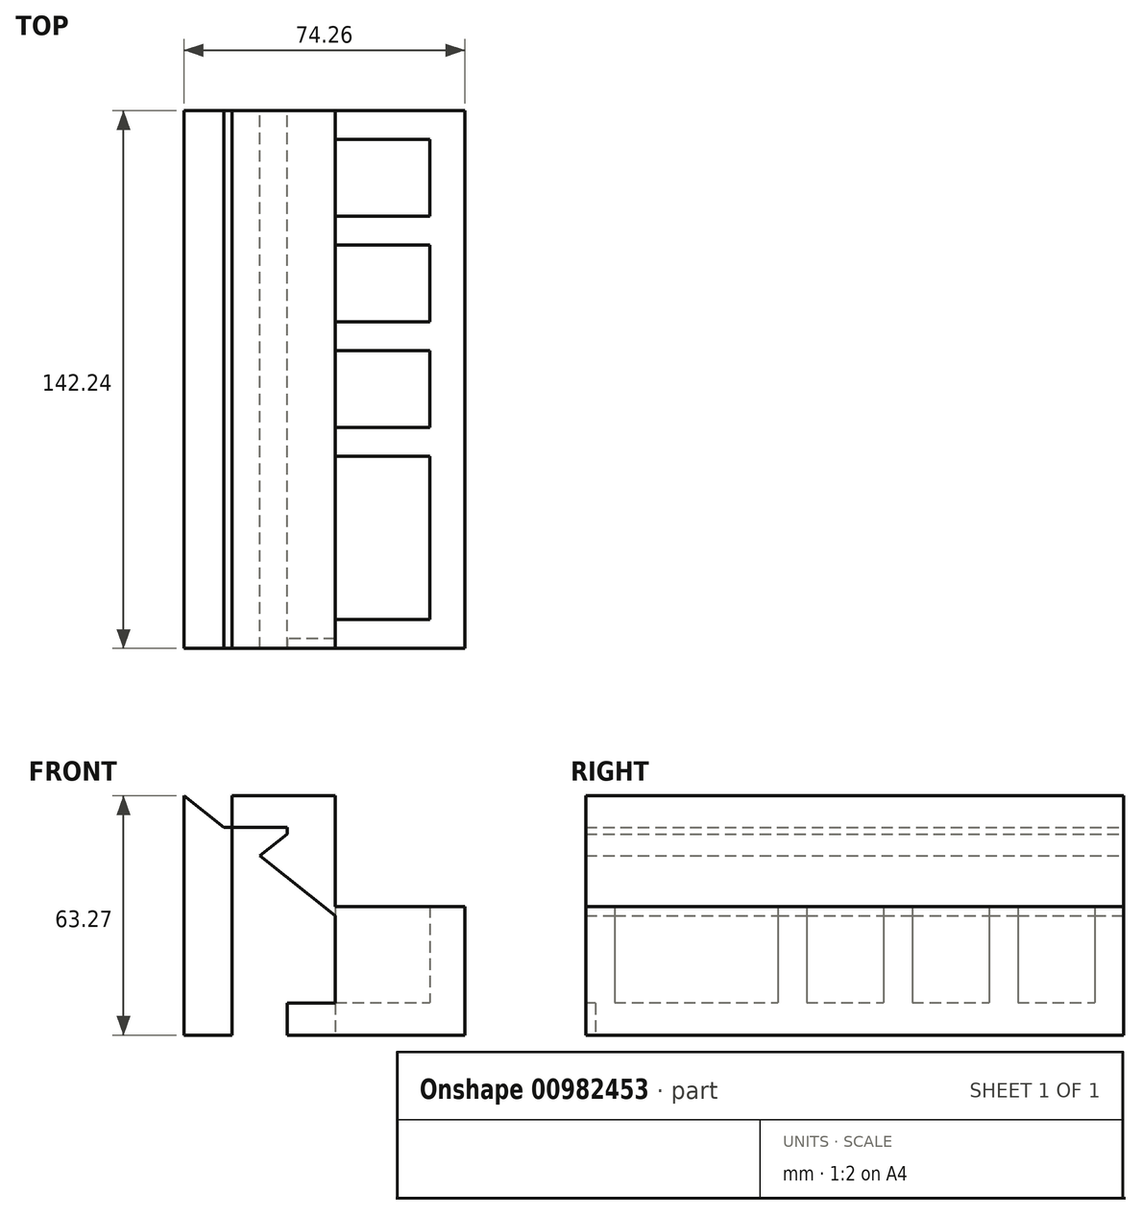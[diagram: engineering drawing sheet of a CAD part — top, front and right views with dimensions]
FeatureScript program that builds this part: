
annotation { "Feature Type Name" : "Feature", "Feature Type Description" : "" }
export const myFeature = defineFeature(function(context is Context, id is Id, definition is map)
    precondition{}
    {
        {
            var Q0;
            Q0=qCreatedBy(makeId("Front.planeOp"),FACE);
            var sketch = newSketch(context, id + "F0", { "sketchPlane" : qUnion([Q0])});
            skLineSegment(sketch, "E0.bottom", {"start": v(-54.43, 16.05) * mm, "end": v(-67.13, 16.05) * mm});
            skLineSegment(sketch, "E0.top", {"start": v(-54.43, 63.27) * mm, "end": v(-67.13, 63.27) * mm});
            skLineSegment(sketch, "E0.left", {"start": v(-54.43, 16.05) * mm, "end": v(-54.43, 63.27) * mm});
            skLineSegment(sketch, "E0.right", {"start": v(-67.13, 16.05) * mm, "end": v(-67.13, 63.27) * mm});
            skLineSegment(sketch, "E1.bottom", {"start": v(-67.13, 63.27) * mm, "end": v(-27.13, 63.27) * mm});
            skLineSegment(sketch, "E1.top", {"start": v(-67.13, 54.94) * mm, "end": v(-27.13, 54.94) * mm});
            skLineSegment(sketch, "E1.left", {"start": v(-67.13, 63.27) * mm, "end": v(-67.13, 54.94) * mm});
            skLineSegment(sketch, "E1.right", {"start": v(-27.13, 63.27) * mm, "end": v(-27.13, 54.94) * mm});
            skLineSegment(sketch, "E2.bottom", {"start": v(-27.13, 63.27) * mm, "end": v(-39.83, 63.27) * mm});
            skLineSegment(sketch, "E2.left", {"start": v(-27.13, 63.27) * mm, "end": v(-27.13, 0) * mm});
            skLineSegment(sketch, "E2.right", {"start": v(-39.83, 63.27) * mm, "end": v(-39.83, 0) * mm});
            skLineSegment(sketch, "E3.left", {"start": v(-39.83, 0) * mm, "end": v(-39.83, 8.64) * mm});
            skLineSegment(sketch, "E3.right", {"start": v(-2.13, 1.02) * mm, "end": v(-2.13, 8.64) * mm});
            skLineSegment(sketch, "E4.top", {"start": v(-2.13, 34.04) * mm, "end": v(7.13, 34.04) * mm});
            skLineSegment(sketch, "E4.left", {"start": v(-2.13, 1.02) * mm, "end": v(-2.13, 34.04) * mm});
            skLineSegment(sketch, "E4.right", {"start": v(7.13, 1.02) * mm, "end": v(7.13, 34.04) * mm});
            skLineSegment(sketch, "E5", {"start": v(-27.13, 8.64) * mm, "end": v(-2.13, 8.64) * mm});
            skLineSegment(sketch, "E6.bottom", {"start": v(-67.13, 63.27) * mm, "end": v(-54.4, 63.27) * mm});
            skLineSegment(sketch, "E7", {"start": v(-67.13, 0) * mm, "end": v(-67.13, 63.27) * mm});
            skLineSegment(sketch, "E8", {"start": v(-54.4, 63.27) * mm, "end": v(-54.4, 0) * mm});
            skLineSegment(sketch, "E9", {"start": v(-54.4, 0) * mm, "end": v(-54.4, 63.27) * mm});
            skLineSegment(sketch, "E10", {"start": v(-67.13, 0) * mm, "end": v(-54.4, 0) * mm});
            skLineSegment(sketch, "E11", {"start": v(-27.13, 63.27) * mm, "end": v(-67.13, 31.64) * mm});
            skLineSegment(sketch, "E12", {"start": v(-67.13, 31.64) * mm, "end": v(-67.13, 63.27) * mm});
            skLineSegment(sketch, "E13", {"start": v(-67.13, 63.27) * mm, "end": v(-27.13, 31.64) * mm});
            skLineSegment(sketch, "E14", {"start": v(-39.83, 0) * mm, "end": v(7.13, 0) * mm});
            skLineSegment(sketch, "E15", {"start": v(7.13, 0) * mm, "end": v(7.13, 34.04) * mm});
            skLineSegment(sketch, "E16", {"start": v(-2.13, 8.64) * mm, "end": v(-2.13, 0) * mm});
            skSolve(sketch);
        }
        {
            var Q0;
            {var subQ5=sQuery(id+"F0.wireOp",EDGE,"E9");var subQ6=sQuery(id+"F0.wireOp",EDGE,"E1.top");var subQ7=makeQuery(id+"F0.imprint","INTERSECT",VERTEX,{"derivedFrom":[subQ6,subQ5]});Q0=makeQuery(id+"F0.imprint","IMPRINT",FACE,{"disambiguationData":[TD([[makeQuery(id+"F0.imprint","IMPRINT",EDGE,{"disambiguationData":[TD([[subQ7,-1.0]])],"derivedFrom":subQ6}),-1.0]])]});}
            var Q1;
            {var subQ1=sQuery(id+"F0.wireOp",EDGE,"E4.top");Q1=makeQuery(id+"F0.imprint","IMPRINT",FACE,{"disambiguationData":[TD([[makeQuery(id+"F0.imprint","IMPRINT",EDGE,{"derivedFrom":subQ1}),-1.0]])]});}
            var Q2;
            {var subQ1=sQuery(id+"F0.wireOp",EDGE,"E1.top");var subQ7=sQuery(id+"F0.wireOp",EDGE,"E2.left");var subQ9=makeQuery(id+"F0.imprint","INTERSECT",VERTEX,{"derivedFrom":[subQ1,subQ7]});Q2=makeQuery(id+"F0.imprint","IMPRINT",FACE,{"disambiguationData":[TD([[makeQuery(id+"F0.imprint","IMPRINT",EDGE,{"disambiguationData":[TD([[subQ9,1.0]])],"derivedFrom":subQ1}),-1.0]])]});}
            var Q3;
            {var subQ3=sQuery(id+"F0.wireOp",EDGE,"E11");var subQ5=sQuery(id+"F0.wireOp",EDGE,"E0.left");var subQ6=makeQuery(id+"F0.imprint","INTERSECT",VERTEX,{"derivedFrom":[subQ5,subQ3]});Q3=makeQuery(id+"F0.imprint","IMPRINT",FACE,{"disambiguationData":[TD([[makeQuery(id+"F0.imprint","IMPRINT",EDGE,{"disambiguationData":[TD([[subQ6,-1.0]])],"derivedFrom":subQ5}),1.0]])]});}
            var Q4;
            {var subQ0=sQuery(id+"F0.wireOp",EDGE,"E11");var subQ1=sQuery(id+"F0.wireOp",EDGE,"E9");var subQ2=makeQuery(id+"F0.imprint","INTERSECT",VERTEX,{"derivedFrom":[subQ1,subQ0]});Q4=makeQuery(id+"F0.imprint","IMPRINT",FACE,{"disambiguationData":[TD([[makeQuery(id+"F0.imprint","IMPRINT",EDGE,{"disambiguationData":[TD([[subQ2,-1.0]])],"derivedFrom":subQ1}),-1.0]])]});}
            var Q5;
            {var subQ0=sQuery(id+"F0.wireOp",EDGE,"E12");var subQ1=sQuery(id+"F0.wireOp",EDGE,"E1.top");var subQ2=makeQuery(id+"F0.imprint","INTERSECT",VERTEX,{"derivedFrom":[subQ1,subQ0]});Q5=makeQuery(id+"F0.imprint","IMPRINT",FACE,{"disambiguationData":[TD([[makeQuery(id+"F0.imprint","IMPRINT",EDGE,{"disambiguationData":[TD([[subQ2,-1.0]])],"derivedFrom":subQ1}),1.0]])]});}
            var Q6;
            {var subQ0=sQuery(id+"F0.wireOp",EDGE,"E0.bottom");Q6=makeQuery(id+"F0.imprint","IMPRINT",FACE,{"disambiguationData":[TD([[makeQuery(id+"F0.imprint","IMPRINT",EDGE,{"derivedFrom":subQ0}),-1.0]])]});}
            var Q7;
            {var subQ5=sQuery(id+"F0.wireOp",EDGE,"E2.bottom");Q7=makeQuery(id+"F0.imprint","IMPRINT",FACE,{"disambiguationData":[TD([[makeQuery(id+"F0.imprint","IMPRINT",EDGE,{"derivedFrom":subQ5}),1.0]])]});}
            var Q8;
            {var subQ0=sQuery(id+"F0.wireOp",EDGE,"E13");var subQ1=sQuery(id+"F0.wireOp",EDGE,"E2.right");var subQ2=makeQuery(id+"F0.imprint","INTERSECT",VERTEX,{"derivedFrom":[subQ1,subQ0]});Q8=makeQuery(id+"F0.imprint","IMPRINT",FACE,{"disambiguationData":[TD([[makeQuery(id+"F0.imprint","IMPRINT",EDGE,{"disambiguationData":[TD([[subQ2,1.0]])],"derivedFrom":subQ1}),-1.0]])]});}
            var Q9;
            {var subQ0=sQuery(id+"F0.wireOp",EDGE,"E5");Q9=makeQuery(id+"F0.imprint","IMPRINT",FACE,{"disambiguationData":[TD([[makeQuery(id+"F0.imprint","IMPRINT",EDGE,{"derivedFrom":subQ0}),-1.0]])]});}
            var Q10;
            {var subQ0=sQuery(id+"F0.wireOp",EDGE,"E2.left");var subQ1=sQuery(id+"F0.wireOp",EDGE,"E1.top");var subQ2=makeQuery(id+"F0.imprint","INTERSECT",VERTEX,{"derivedFrom":[subQ1,subQ0]});Q10=makeQuery(id+"F0.imprint","IMPRINT",FACE,{"disambiguationData":[TD([[makeQuery(id+"F0.imprint","IMPRINT",EDGE,{"disambiguationData":[TD([[subQ2,1.0]])],"derivedFrom":subQ1}),1.0]])]});}
            var Q11;
            {var subQ0=sQuery(id+"F0.wireOp",EDGE,"E3.left");Q11=makeQuery(id+"F0.imprint","IMPRINT",FACE,{"disambiguationData":[TD([[makeQuery(id+"F0.imprint","IMPRINT",EDGE,{"derivedFrom":subQ0}),-1.0]])]});}
            var Q12;
            {var subQ0=sQuery(id+"F0.wireOp",EDGE,"E6.bottom");var subQ1=sQuery(id+"F0.wireOp",EDGE,"E0.left");var subQ2=makeQuery(id+"F0.imprint","INTERSECT",VERTEX,{"derivedFrom":[subQ1,subQ0]});Q12=makeQuery(id+"F0.imprint","IMPRINT",FACE,{"disambiguationData":[TD([[makeQuery(id+"F0.imprint","IMPRINT",EDGE,{"disambiguationData":[TD([[subQ2,1.0]])],"derivedFrom":subQ1}),1.0]])]});}
            var Q13;
            {var subQ0=sQuery(id+"F0.wireOp",EDGE,"E1.bottom");Q13=makeQuery(id+"F0.imprint","IMPRINT",FACE,{"disambiguationData":[TD([[makeQuery(id+"F0.imprint","IMPRINT",EDGE,{"derivedFrom":subQ0}),-1.0]])]});}
            var Q14;
            {var subQ5=sQuery(id+"F0.wireOp",EDGE,"E0.bottom");Q14=makeQuery(id+"F0.imprint","IMPRINT",FACE,{"disambiguationData":[TD([[makeQuery(id+"F0.imprint","IMPRINT",EDGE,{"derivedFrom":subQ5}),1.0]])]});}
            var Q15;
            {var subQ0=sQuery(id+"F0.wireOp",EDGE,"E13");var subQ1=sQuery(id+"F0.wireOp",EDGE,"E0.left");var subQ2=makeQuery(id+"F0.imprint","INTERSECT",VERTEX,{"derivedFrom":[subQ1,subQ0]});Q15=makeQuery(id+"F0.imprint","IMPRINT",FACE,{"disambiguationData":[TD([[makeQuery(id+"F0.imprint","IMPRINT",EDGE,{"disambiguationData":[TD([[subQ2,-1.0]])],"derivedFrom":subQ1}),1.0]])]});}
            var Q16;
            {var subQ0=sQuery(id+"F0.wireOp",EDGE,"E2.right");var subQ1=sQuery(id+"F0.wireOp",EDGE,"E1.top");var subQ2=makeQuery(id+"F0.imprint","INTERSECT",VERTEX,{"derivedFrom":[subQ1,subQ0]});Q16=makeQuery(id+"F0.imprint","IMPRINT",FACE,{"disambiguationData":[TD([[makeQuery(id+"F0.imprint","IMPRINT",EDGE,{"disambiguationData":[TD([[subQ2,-1.0]])],"derivedFrom":subQ1}),-1.0]])]});}
            var Q17;
            {var subQ0=sQuery(id+"F0.wireOp",EDGE,"E11");var subQ1=sQuery(id+"F0.wireOp",EDGE,"E0.left");var subQ2=makeQuery(id+"F0.imprint","INTERSECT",VERTEX,{"derivedFrom":[subQ1,subQ0]});Q17=makeQuery(id+"F0.imprint","IMPRINT",FACE,{"disambiguationData":[TD([[makeQuery(id+"F0.imprint","IMPRINT",EDGE,{"disambiguationData":[TD([[subQ2,-1.0]])],"derivedFrom":subQ1}),-1.0]])]});}
            var Q18;
            {var subQ0=sQuery(id+"F0.wireOp",EDGE,"E13");var subQ1=sQuery(id+"F0.wireOp",EDGE,"E0.left");var subQ2=makeQuery(id+"F0.imprint","INTERSECT",VERTEX,{"derivedFrom":[subQ1,subQ0]});Q18=makeQuery(id+"F0.imprint","IMPRINT",FACE,{"disambiguationData":[TD([[makeQuery(id+"F0.imprint","IMPRINT",EDGE,{"disambiguationData":[TD([[subQ2,-1.0]])],"derivedFrom":subQ1}),-1.0]])]});}
            var Q19;
            {var subQ0=sQuery(id+"F0.wireOp",EDGE,"E6.bottom");var subQ1=sQuery(id+"F0.wireOp",EDGE,"E0.left");var subQ2=makeQuery(id+"F0.imprint","INTERSECT",VERTEX,{"derivedFrom":[subQ1,subQ0]});Q19=makeQuery(id+"F0.imprint","IMPRINT",FACE,{"disambiguationData":[TD([[makeQuery(id+"F0.imprint","IMPRINT",EDGE,{"disambiguationData":[TD([[subQ2,1.0]])],"derivedFrom":subQ1}),-1.0]])]});}
            extrude(context, id + "F1", {"entities" : qUnion([Q0, Q1, Q2, Q3, Q4, Q5, Q6, Q7, Q8, Q9, Q10, Q11, Q12, Q13, Q14, Q15, Q16, Q17, Q18, Q19]), "depth" : 142.24 * mm, "offsetDistance" : 25.4 * mm});
        }
        {
            var Q0;
            Q0=makeQuery(id+"F1.opExtrude","CAP_FACE",FACE,{"disambiguationData":[OSD([sQuery(id+"F0.wireOp",EDGE,"E0.bottom"),sQuery(id+"F0.wireOp",EDGE,"E0.left"),sQuery(id+"F0.wireOp",EDGE,"E0.right"),sQuery(id+"F0.wireOp",EDGE,"E1.bottom"),sQuery(id+"F0.wireOp",EDGE,"E1.top"),sQuery(id+"F0.wireOp",EDGE,"E1.left"),sQuery(id+"F0.wireOp",EDGE,"E2.bottom"),sQuery(id+"F0.wireOp",EDGE,"E2.left"),sQuery(id+"F0.wireOp",EDGE,"E2.right"),sQuery(id+"F0.wireOp",EDGE,"E3.bottom"),sQuery(id+"F0.wireOp",EDGE,"E3.top"),sQuery(id+"F0.wireOp",EDGE,"E3.left"),sQuery(id+"F0.wireOp",EDGE,"E4.bottom"),sQuery(id+"F0.wireOp",EDGE,"E4.top"),sQuery(id+"F0.wireOp",EDGE,"E4.left"),sQuery(id+"F0.wireOp",EDGE,"E4.right")])],"isStart":false});
            var sketch = newSketch(context, id + "F2", { "sketchPlane" : qUnion([Q0])});
            skLineSegment(sketch, "E17.bottom", {"start": v(-11.94, 0) * mm, "end": v(-39.83, 0) * mm});
            skLineSegment(sketch, "E17.top", {"start": v(-11.94, 8.44) * mm, "end": v(-39.83, 8.44) * mm});
            skLineSegment(sketch, "E17.left", {"start": v(-11.94, 0) * mm, "end": v(-11.94, 8.44) * mm});
            skLineSegment(sketch, "E17.right", {"start": v(-39.83, 0) * mm, "end": v(-39.83, 8.44) * mm});
            skSolve(sketch);
        }
        {
            var Q0;
            Q0 = qSketchRegion(id + "F2", true);
            extrude(context, id + "F3", {"entities" : qUnion([Q0]), "operationType" : NewBodyOperationType.ADD, "depth" : -2.54 * mm, "offsetDistance" : 25.4 * mm});
        }
        {
            var Q0;
            Q0=makeQuery(id+"F1.opExtrude","SWEPT_FACE",FACE,{"disambiguationData":[OSD([sQuery(id+"F0.wireOp",EDGE,"E5")])]});
            var sketch = newSketch(context, id + "F4", { "sketchPlane" : qUnion([Q0])});
            skLineSegment(sketch, "E18.bottom", {"start": v(-2.13, -83.82) * mm, "end": v(-27.13, -83.82) * mm});
            skLineSegment(sketch, "E18.top", {"start": v(-2.13, -91.44) * mm, "end": v(-27.13, -91.44) * mm});
            skLineSegment(sketch, "E18.left", {"start": v(-2.13, -91.44) * mm, "end": v(-2.13, -83.82) * mm});
            skLineSegment(sketch, "E18.right", {"start": v(-27.13, -91.44) * mm, "end": v(-27.13, -83.82) * mm});
            skLineSegment(sketch, "E19", {"start": v(-27.13, -91.44) * mm, "end": v(-27.13, -63.5) * mm});
            skLineSegment(sketch, "E20.bottom", {"start": v(-27.13, -63.5) * mm, "end": v(-2.13, -63.5) * mm});
            skLineSegment(sketch, "E20.top", {"start": v(-27.13, -55.88) * mm, "end": v(-2.13, -55.88) * mm});
            skLineSegment(sketch, "E20.left", {"start": v(-27.13, -63.5) * mm, "end": v(-27.13, -55.88) * mm});
            skLineSegment(sketch, "E20.right", {"start": v(-2.13, -63.5) * mm, "end": v(-2.13, -55.88) * mm});
            skLineSegment(sketch, "E21.top", {"start": v(-27.13, -7.62) * mm, "end": v(-2.13, -7.62) * mm});
            skLineSegment(sketch, "E21.left", {"start": v(-27.13, -55.88) * mm, "end": v(-27.13, -7.62) * mm});
            skLineSegment(sketch, "E22.top", {"start": v(-27.13, 0) * mm, "end": v(-2.13, 0) * mm});
            skLineSegment(sketch, "E22.left", {"start": v(-27.13, -7.62) * mm, "end": v(-27.13, 0) * mm});
            skLineSegment(sketch, "E22.right", {"start": v(-2.13, -7.62) * mm, "end": v(-2.13, 0) * mm});
            skLineSegment(sketch, "E23", {"start": v(-2.13, -83.82) * mm, "end": v(-2.13, -142.24) * mm});
            skLineSegment(sketch, "E24", {"start": v(-2.13, -83.82) * mm, "end": v(-2.13, -139.7) * mm});
            skLineSegment(sketch, "E25", {"start": v(-2.13, -83.82) * mm, "end": v(-2.13, -63.5) * mm});
            skLineSegment(sketch, "E26.bottom", {"start": v(-27.13, -35.56) * mm, "end": v(-2.13, -35.56) * mm});
            skLineSegment(sketch, "E26.top", {"start": v(-27.13, -27.94) * mm, "end": v(-2.13, -27.94) * mm});
            skLineSegment(sketch, "E26.left", {"start": v(-27.13, -35.56) * mm, "end": v(-27.13, -27.94) * mm});
            skLineSegment(sketch, "E26.right", {"start": v(-2.13, -35.56) * mm, "end": v(-2.13, -27.94) * mm});
            skLineSegment(sketch, "E27", {"start": v(-2.13, -55.88) * mm, "end": v(-2.13, -35.56) * mm});
            skLineSegment(sketch, "E28", {"start": v(-2.13, -27.94) * mm, "end": v(-2.13, -7.62) * mm});
            skLineSegment(sketch, "E29", {"start": v(-2.13, -142.24) * mm, "end": v(-2.13, -134.62) * mm});
            skLineSegment(sketch, "E30.bottom", {"start": v(-2.13, -134.62) * mm, "end": v(-27.13, -134.62) * mm});
            skLineSegment(sketch, "E30.top", {"start": v(-2.13, -142.78) * mm, "end": v(-27.13, -142.78) * mm});
            skLineSegment(sketch, "E30.left", {"start": v(-2.13, -134.62) * mm, "end": v(-2.13, -142.78) * mm});
            skLineSegment(sketch, "E30.right", {"start": v(-27.13, -134.62) * mm, "end": v(-27.13, -142.78) * mm});
            skSolve(sketch);
        }
        {
            var Q0;
            Q0=makeQuery(id+"F4.imprint","IMPRINT",FACE,{"disambiguationData":[TD([[makeQuery(id+"F4.imprint","IMPRINT",EDGE,{"derivedFrom":sQuery(id+"F4.wireOp",EDGE,"E18.bottom")}),1.0]])]});
            var Q1;
            Q1=makeQuery(id+"F4.imprint","IMPRINT",FACE,{"disambiguationData":[TD([[makeQuery(id+"F4.imprint","IMPRINT",EDGE,{"derivedFrom":sQuery(id+"F4.wireOp",EDGE,"E20.bottom")}),1.0]])]});
            var Q2;
            {var subQ0=sQuery(id+"F4.wireOp",EDGE,"E26.bottom");Q2=makeQuery(id+"F4.imprint","IMPRINT",FACE,{"disambiguationData":[TD([[makeQuery(id+"F4.imprint","IMPRINT",EDGE,{"derivedFrom":subQ0}),1.0]])]});}
            var Q3;
            Q3=makeQuery(id+"F4.imprint","IMPRINT",FACE,{"disambiguationData":[TD([[makeQuery(id+"F4.imprint","IMPRINT",EDGE,{"derivedFrom":sQuery(id+"F4.wireOp",EDGE,"E21.top")}),1.0]])]});
            var Q4;
            {var subQ3=sQuery(id+"F4.wireOp",EDGE,"E30.bottom");Q4=makeQuery(id+"F4.imprint","IMPRINT",FACE,{"disambiguationData":[TD([[makeQuery(id+"F4.imprint","IMPRINT",EDGE,{"derivedFrom":subQ3}),1.0]])]});}
            extrude(context, id + "F5", {"entities" : qUnion([Q0, Q1, Q2, Q3, Q4]), "operationType" : NewBodyOperationType.ADD, "depth" : 25.4 * mm, "offsetDistance" : 25.4 * mm});
        }
    });
